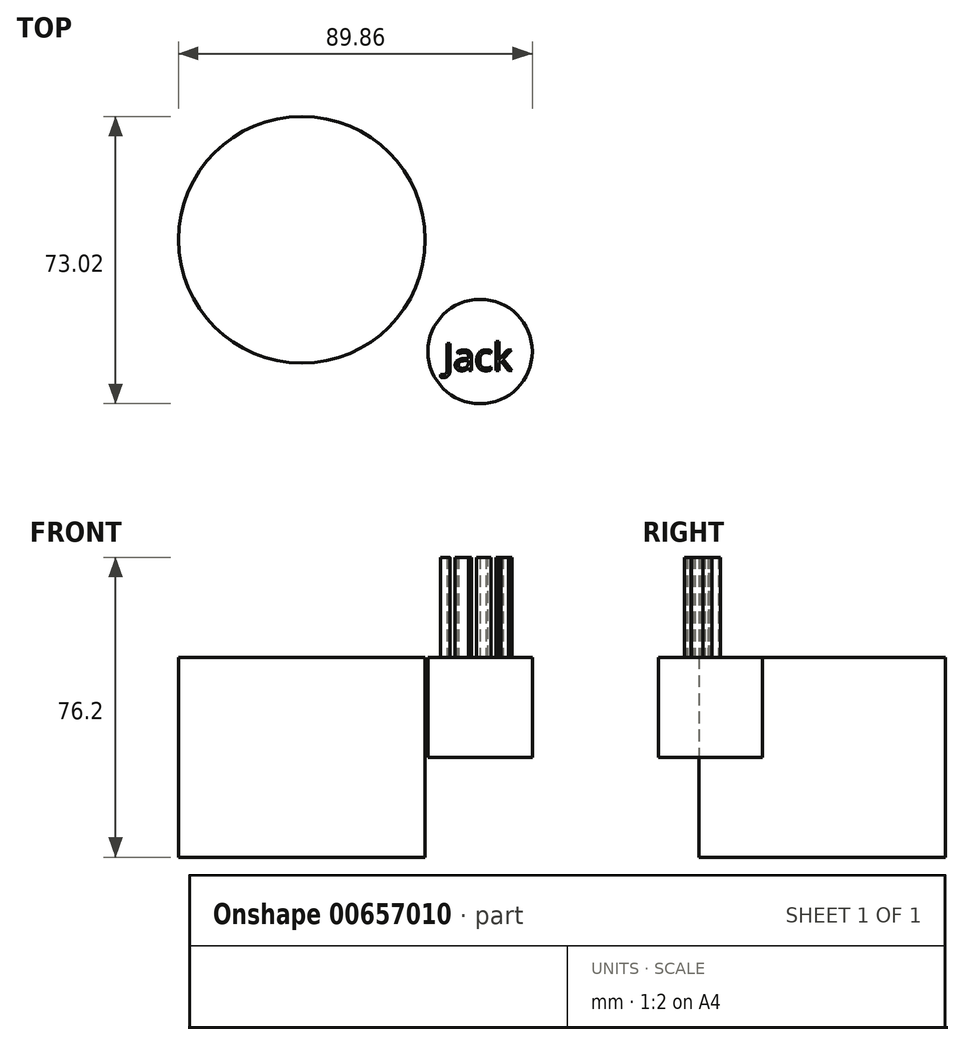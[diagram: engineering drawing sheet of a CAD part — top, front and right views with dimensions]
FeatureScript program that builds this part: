
annotation { "Feature Type Name" : "Feature", "Feature Type Description" : "" }
export const myFeature = defineFeature(function(context is Context, id is Id, definition is map)
    precondition{}
    {
        {
            var Q0;
            Q0=qCreatedBy(makeId("Top.planeOp"),FACE);
            var sketch = newSketch(context, id + "F0", { "sketchPlane" : qUnion([Q0])});
            skCircle(sketch, "E0", {"center": v(0, 0) * mm, "radius": 31.33 * mm});
            skSolve(sketch);
        }
        {
            var Q0;
            Q0 = qSketchRegion(id + "F0", true);
            extrude(context, id + "F1", {"entities" : qUnion([Q0]), "depth" : 25.4 * mm, "offsetDistance" : 25.4 * mm});
        }
        {
            var Q0;
            Q0=qCreatedBy(makeId("Top.planeOp"),FACE);
            var sketch = newSketch(context, id + "F2", { "sketchPlane" : qUnion([Q0])});
            skArc(sketch, "E1", {"start": v(-39.55, -47.98) * mm, "mid": v(0.64, -66.14) * mm, "end": v(41.96, -50.68) * mm});
            skSolve(sketch);
        }
        {
            var Q0;
            Q0 = qSketchRegion(id + "F2", true);
            var Q1;
            Q1=makeQuery(id+"F1.opExtrude","CAP_FACE",FACE,{"disambiguationData":[OSD([sQuery(id+"F0.wireOp",EDGE,"E0")])],"isStart":true});
            extrude(context, id + "F3", {"entities" : qUnion([Q0, Q1]), "operationType" : NewBodyOperationType.ADD, "depth" : 25.4 * mm, "offsetDistance" : 25.4 * mm});
        }
        {
            var Q0;
            Q0=qCreatedBy(makeId("Top.planeOp"),FACE);
            var sketch = newSketch(context, id + "F4", { "sketchPlane" : qUnion([Q0])});
            skCircle(sketch, "E2", {"center": v(-56.7, -28.42) * mm, "radius": 13.3 * mm});
            skCircle(sketch, "E3", {"center": v(45.27, -28.42) * mm, "radius": 13.27 * mm});
            skSolve(sketch);
        }
        {
            var Q0;
            Q0=makeQuery(id+"F4.imprint","IMPRINT",FACE,{"disambiguationData":[TD([[makeQuery(id+"F4.imprint","IMPRINT",EDGE,{"derivedFrom":sQuery(id+"F4.wireOp",EDGE,"E3")}),1.0]])]});
            extrude(context, id + "F5", {"entities" : qUnion([Q0]), "depth" : 25.4 * mm, "offsetDistance" : 25.4 * mm});
        }
        {
            var Q0;
            Q0=makeQuery(id+"F5.opExtrude","CAP_FACE",FACE,{"disambiguationData":[OSD([sQuery(id+"F4.wireOp",EDGE,"E3")])],"isStart":false});
            var sketch = newSketch(context, id + "F6", { "sketchPlane" : qUnion([Q0])});
            skText(sketch, "E4", { "text": "Jack", "fontName": "OpenSans-Regular.ttf"});
            const initialGuessF6  = {"E4": [0.03594, -0.03324, 1, 0, 0.00692]};
            skSetInitialGuess(sketch, initialGuessF6);
            skSolve(sketch);
        }
        {
            var Q0;
            Q0 = qSketchRegion(id + "F6", true);
            extrude(context, id + "F7", {"entities" : qUnion([Q0]), "operationType" : NewBodyOperationType.ADD, "depth" : 25.4 * mm, "offsetDistance" : 25.4 * mm});
        }
    });
